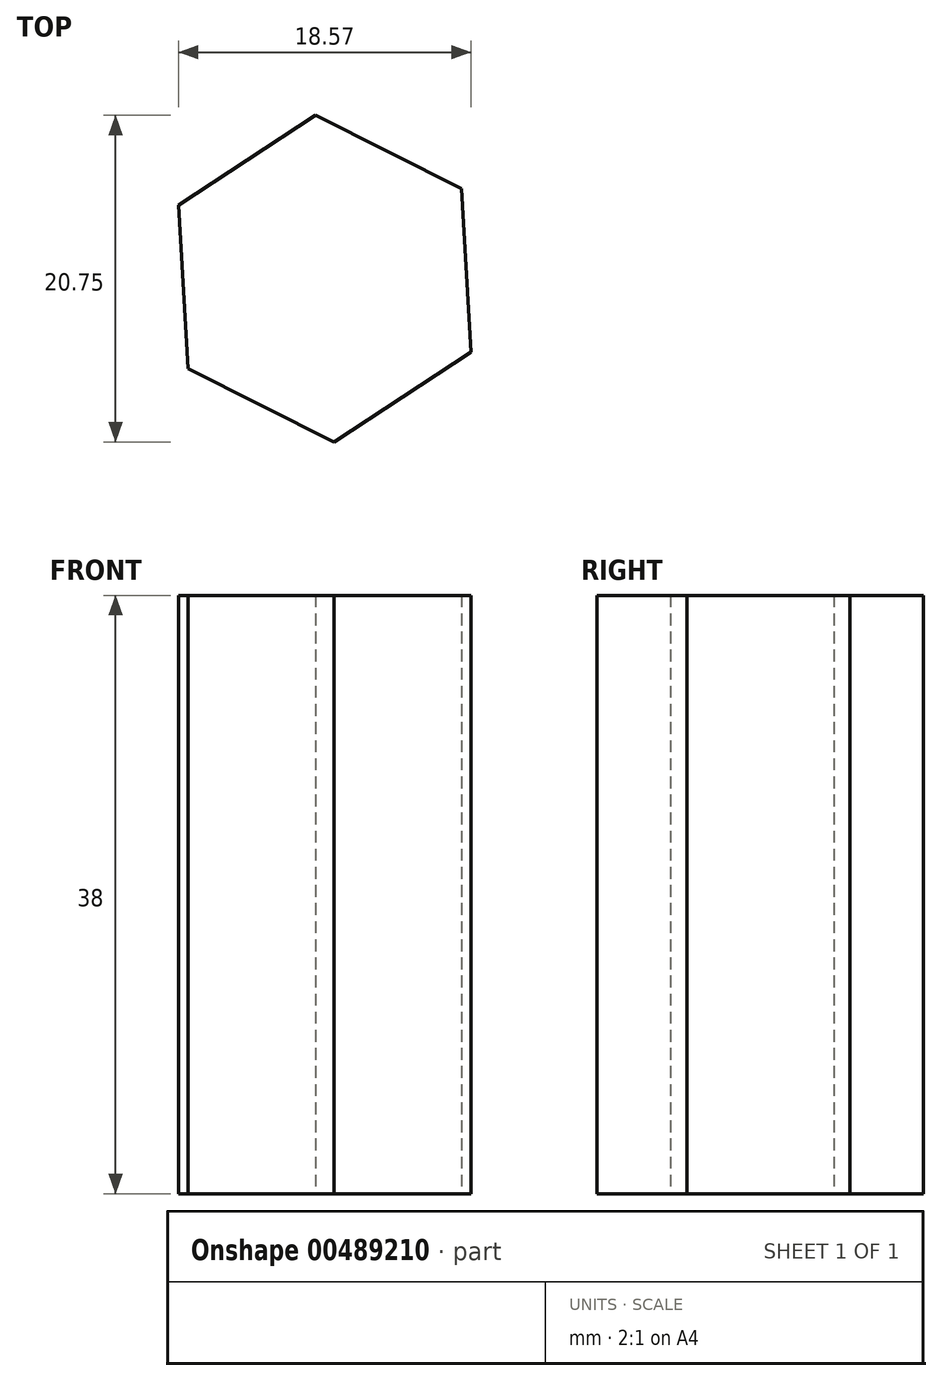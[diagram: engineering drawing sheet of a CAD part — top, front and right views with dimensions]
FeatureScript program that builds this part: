
annotation { "Feature Type Name" : "Feature", "Feature Type Description" : "" }
export const myFeature = defineFeature(function(context is Context, id is Id, definition is map)
    precondition{}
    {
        {
            var Q0;
            Q0=qCreatedBy(makeId("Top.planeOp"),FACE);
            var sketch = newSketch(context, id + "F0", { "sketchPlane" : qUnion([Q0])});
            skCircle(sketch, "E0.cCircle", {"center": v(6.82, -29.2) * mm, "radius": 9 * mm, "construction": true});
            skLineSegment(sketch, "E0.0", {"start": v(6.22, -18.83) * mm, "end": v(15.5, -23.5) * mm});
            skLineSegment(sketch, "E0.1", {"start": v(15.5, -23.5) * mm, "end": v(16.1, -33.88) * mm});
            skLineSegment(sketch, "E0.2", {"start": v(16.1, -33.88) * mm, "end": v(7.41, -39.58) * mm});
            skLineSegment(sketch, "E0.3", {"start": v(7.41, -39.58) * mm, "end": v(-1.87, -34.91) * mm});
            skLineSegment(sketch, "E0.4", {"start": v(-1.87, -34.91) * mm, "end": v(-2.47, -24.54) * mm});
            skLineSegment(sketch, "E0.5", {"start": v(-2.47, -24.54) * mm, "end": v(6.22, -18.83) * mm});
            skPoint(sketch, "E0.0.midPoint", {"position": v(10.86, -21.17) * mm});
            skSolve(sketch);
        }
        {
            var Q0;
            Q0=makeQuery(id+"F0.imprint","IMPRINT",FACE,{"disambiguationData":[TD([[makeQuery(id+"F0.imprint","IMPRINT",EDGE,{"derivedFrom":sQuery(id+"F0.wireOp",EDGE,"E0.0")}),-1.0]])]});
            extrude(context, id + "F1", {"entities" : qUnion([Q0]), "depth" : 38 * mm});
        }
    });
